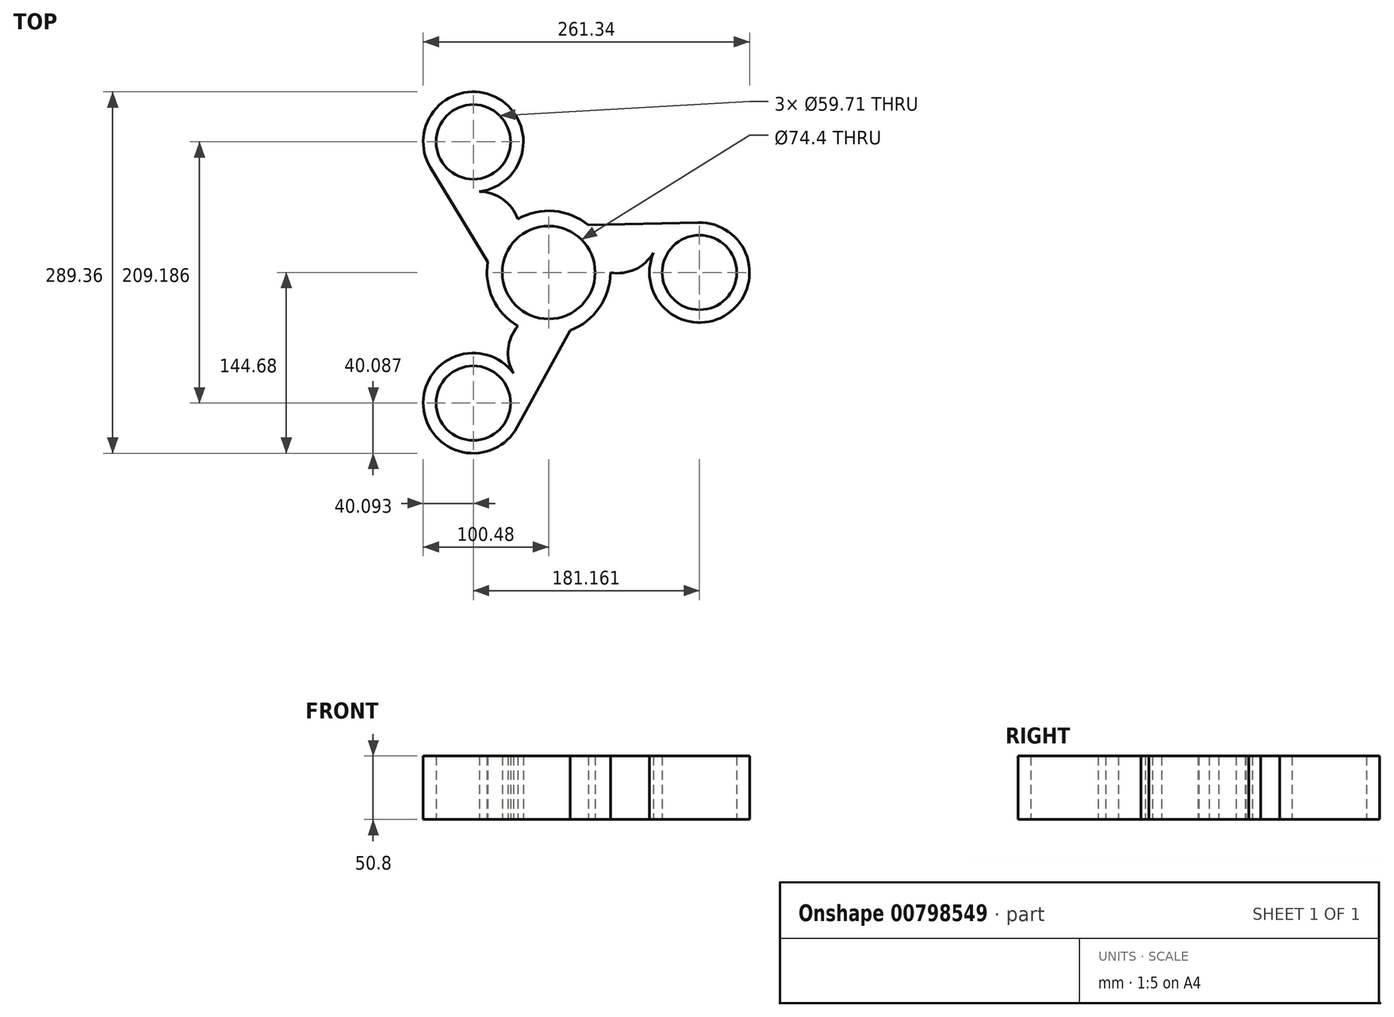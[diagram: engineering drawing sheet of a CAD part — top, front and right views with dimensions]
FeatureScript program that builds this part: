
annotation { "Feature Type Name" : "Feature", "Feature Type Description" : "" }
export const myFeature = defineFeature(function(context is Context, id is Id, definition is map)
    precondition{}
    {
        {
            var Q0;
            Q0=qCreatedBy(makeId("Top.planeOp"),FACE);
            var sketch = newSketch(context, id + "F0", { "sketchPlane" : qUnion([Q0])});
            skCircle(sketch, "E0", {"center": v(0, 0) * mm, "radius": 49.43 * mm});
            skCircle(sketch, "E1", {"center": v(0, 0) * mm, "radius": 37.2 * mm});
            skCircle(sketch, "E2", {"center": v(120.77, 0) * mm, "radius": 40.1 * mm});
            skLineSegment(sketch, "E3", {"start": v(0, 37.2) * mm, "end": v(119.81, 40.08) * mm});
            skCircle(sketch, "E4.1.0", {"center": v(-60.39, 104.6) * mm, "radius": 40.1 * mm});
            skCircle(sketch, "E4.2.0", {"center": v(-60.39, -104.6) * mm, "radius": 40.1 * mm});
            skLineSegment(sketch, "E5.1.0", {"start": v(-32.22, -18.6) * mm, "end": v(-94.61, 83.72) * mm});
            skLineSegment(sketch, "E5.2.0", {"start": v(32.22, -18.6) * mm, "end": v(-25.2, -123.8) * mm});
            skArc(sketch, "E6", {"start": v(49.43, 0) * mm, "mid": v(71.28, 3.56) * mm, "end": v(86.05, 20.04) * mm});
            skArc(sketch, "E7.1.0", {"start": v(-24.71, 42.8) * mm, "mid": v(-38.72, 59.95) * mm, "end": v(-60.39, 64.5) * mm});
            skArc(sketch, "E7.2.0", {"start": v(-24.71, -42.8) * mm, "mid": v(-32.55, -63.5) * mm, "end": v(-25.67, -84.55) * mm});
            skCircle(sketch, "E8", {"center": v(120.77, 0) * mm, "radius": 29.85 * mm});
            skCircle(sketch, "E9.1.1", {"center": v(-60.39, 104.6) * mm, "radius": 29.85 * mm});
            skCircle(sketch, "E9.2.1", {"center": v(-60.39, -104.6) * mm, "radius": 29.85 * mm});
            skSolve(sketch);
        }
        {
            var Q0;
            Q0 = qSketchRegion(id + "F0", true);
            var Q1;
            Q1=sQuery(id+"F0.wireOp",EDGE,"E4.2.0");
            extrude(context, id + "F1", {"entities" : qUnion([Q0]), "surfaceEntities" : qUnion([Q1]), "depth" : 25.4 * mm, "offsetDistance" : 25.4 * mm});
        }
        {
            var Q0;
            Q0=makeQuery(id+"F1.opExtrude","CAP_FACE",FACE,{"disambiguationData":[OSD([sQuery(id+"F0.wireOp",EDGE,"E0"),sQuery(id+"F0.wireOp",EDGE,"E1"),sQuery(id+"F0.wireOp",EDGE,"E2"),sQuery(id+"F0.wireOp",EDGE,"E3"),sQuery(id+"F0.wireOp",EDGE,"E5.1.0"),sQuery(id+"F0.wireOp",EDGE,"E5.2.0"),sQuery(id+"F0.wireOp",EDGE,"E6"),sQuery(id+"F0.wireOp",EDGE,"E7.1.0"),sQuery(id+"F0.wireOp",EDGE,"E7.2.0"),sQuery(id+"F0.wireOp",EDGE,"E8"),sQuery(id+"F0.wireOp",EDGE,"E4.1.0"),sQuery(id+"F0.wireOp",EDGE,"E9.1.1"),sQuery(id+"F0.wireOp",EDGE,"E4.2.0"),sQuery(id+"F0.wireOp",EDGE,"E9.2.1")])],"isStart":false});
            extrude(context, id + "F2", {"entities" : qUnion([Q0]), "operationType" : NewBodyOperationType.ADD, "depth" : 25.4 * mm, "offsetDistance" : 25.4 * mm});
        }
    });
